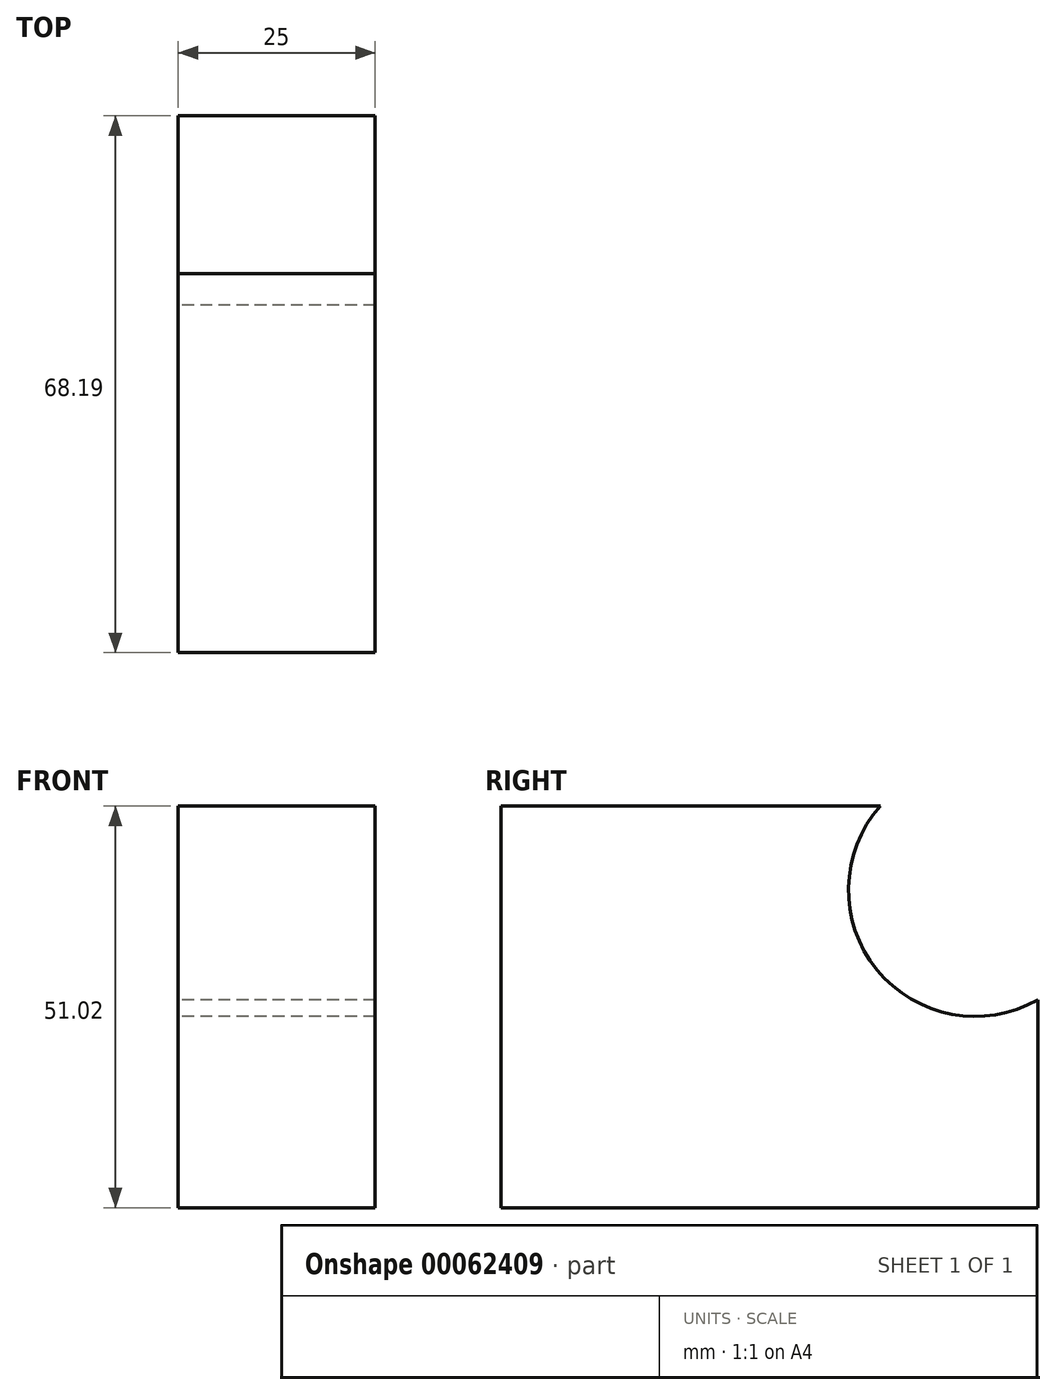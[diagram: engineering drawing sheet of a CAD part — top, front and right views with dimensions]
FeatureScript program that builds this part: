
annotation { "Feature Type Name" : "Feature", "Feature Type Description" : "" }
export const myFeature = defineFeature(function(context is Context, id is Id, definition is map)
    precondition{}
    {
        {
            var Q0;
            Q0=qCreatedBy(makeId("Right.planeOp"),FACE);
            var sketch = newSketch(context, id + "F0", { "sketchPlane" : qUnion([Q0])});
            skLineSegment(sketch, "E0.bottom", {"start": v(-37.72, -15.35) * mm, "end": v(30.47, -15.35) * mm});
            skLineSegment(sketch, "E0.top", {"start": v(-37.72, 35.67) * mm, "end": v(10.44, 35.67) * mm});
            skLineSegment(sketch, "E0.left", {"start": v(-37.72, -15.35) * mm, "end": v(-37.72, 35.67) * mm});
            skLineSegment(sketch, "E0.right", {"start": v(30.47, -15.35) * mm, "end": v(30.47, 11.07) * mm});
            skArc(sketch, "E1", {"start": v(10.44, 35.67) * mm, "mid": v(10.02, 14.87) * mm, "end": v(30.47, 11.07) * mm});
            skSolve(sketch);
        }
        {
            var Q0;
            Q0=makeQuery(id+"F0.imprint","IMPRINT",FACE,{"disambiguationData":[TD([[makeQuery(id+"F0.imprint","IMPRINT",EDGE,{"derivedFrom":sQuery(id+"F0.wireOp",EDGE,"E0.bottom")}),1.0]])]});
            extrude(context, id + "F1", {"entities" : qUnion([Q0]), "depth" : 25 * mm});
        }
    });
